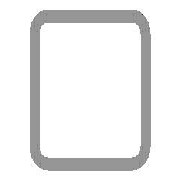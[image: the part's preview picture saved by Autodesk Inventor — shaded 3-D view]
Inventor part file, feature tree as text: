
AUTODESK INVENTOR PART (.ipt)
format: ipt  version: 2024.2 (Build 282272000, 272)  size: 128,512 bytes
history: native  units: mm (DEFAULTED — no unit token found)
features: other x4, sketch x1, plane x1
ambient origin geometry x8: Origin, YZ Plane, XZ Plane, XY Plane, X Axis, Y Axis, Z Axis, Center Point
bodies: Solid1 (feature_tree), Body (feature_tree)
feature tree (6):
  parser-record x1  (decoder bookkeeping rows leaked as tree rows — omitted from the tree; the rows remain in map.json)
  other  "Driven Length"
  other  "Start Plane"
  other  "End Plane"
  sketch  "Sketch3"  dims[d3=90.0mm d4=0.0mm d7=4.0mm d9=40.0mm d11=40.0mm d12=2.0mm d13=50.0mm d14=140.0mm d15=20.0mm d16=20.0mm d17=90.0deg d18=90.0mm]
  plane  "Work Plane3"
